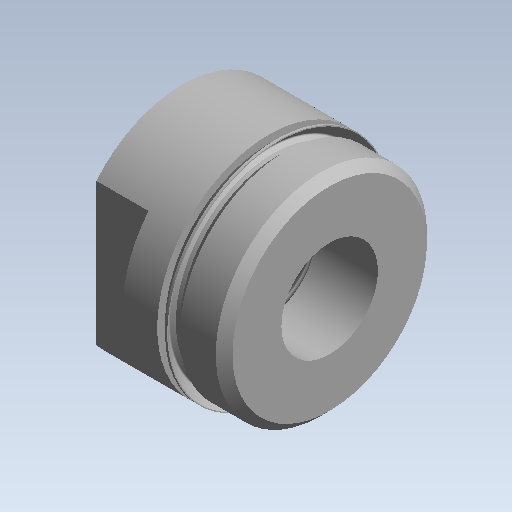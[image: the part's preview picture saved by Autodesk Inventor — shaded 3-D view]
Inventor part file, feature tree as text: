
AUTODESK INVENTOR PART (.ipt)
format: ipt  version: 2020 (Build 240168000, 168)  size: 226,304 bytes
history: native  units: mm (DEFAULTED — no unit token found)
features: other x126, sketch x4, revolve x3, thread x1, extrude x1
ambient origin geometry x8: Origin, YZ Plane, XZ Plane, XY Plane, X Axis, Y Axis, Z Axis, Center Point
bodies: Solid1 (feature_tree)
feature tree (135):
  revolve  "Revolution1"  Angle=360.0deg
  revolve  "Revolution2"  [1 undecoded]
  thread  "Thread1"  [1 undecoded]
  extrude  "Extrusion1"  [1 undecoded]
  revolve  "Revolution3"  [1 undecoded]
  other  "cut1_XY"
  other  "cut1_YZ"
  other  "cut1_ZX"
  other  "cut1_X"
  other  "cut1_Y"
  other  "cut1_Z"
  other  "cut1_Center"
  other  "cut2_XY"
  other  "cut2_YZ"
  other  "cut2_ZX"
  other  "cut2_X"
  other  "cut2_Y"
  other  "cut2_Z"
  other  "cut2_Center"
  other  "cutf1_XY"
  other  "cutf1_YZ"
  other  "cutf1_ZX"
  other  "cutf1_X"
  other  "cutf1_Y"
  other  "cutf1_Z"
  other  "cutf1_Center"
  other  "cutf2_XY"
  other  "cutf2_YZ"
  other  "cutf2_ZX"
  other  "cutf2_X"
  other  "cutf2_Y"
  other  "cutf2_Z"
  other  "cutf2_Center"
  other  "lovra_XY"
  other  "lovra_YZ"
  other  "lovra_ZX"
  other  "lovra_X"
  other  "lovra_Y"
  other  "lovra_Z"
  other  "lovra_Center"
  other  "lovra1_XY"
  other  "lovra1_YZ"
  other  "lovra1_ZX"
  other  "lovra1_X"
  other  "lovra1_Y"
  other  "lovra1_Z"
  other  "lovra1_Center"
  other  "lovra2_XY"
  other  "lovra2_YZ"
  other  "lovra2_ZX"
  other  "lovra2_X"
  other  "lovra2_Y"
  other  "lovra2_Z"
  other  "lovra2_Center"
  other  "lovra21_XY"
  other  "lovra21_YZ"
  other  "lovra21_ZX"
  other  "lovra21_X"
  other  "lovra21_Y"
  other  "lovra21_Z"
  other  "lovra21_Center"
  other  "lovra22_XY"
  other  "lovra22_YZ"
  other  "lovra22_ZX"
  other  "lovra22_X"
  other  "lovra22_Y"
  other  "lovra22_Z"
  other  "lovra22_Center"
  other  "lovra3_XY"
  other  "lovra3_YZ"
  other  "lovra3_ZX"
  other  "lovra3_X"
  other  "lovra3_Y"
  other  "lovra3_Z"
  other  "lovra3_Center"
  other  "olen_XY"
  other  "olen_YZ"
  other  "olen_ZX"
  other  "olen_X"
  other  "olen_Y"
  other  "olen_Z"
  other  "olen_Center"
  other  "to_mounting_bracket_XY"
  other  "to_mounting_bracket_YZ"
  other  "to_mounting_bracket_ZX"
  other  "to_mounting_bracket_X"
  other  "to_mounting_bracket_Y"
  other  "to_mounting_bracket_Z"
  other  "to_mounting_bracket_Center"
  other  "to_nut_XY"
  other  "to_nut_YZ"
  other  "to_nut_ZX"
  other  "to_nut_X"
  other  "to_nut_Y"
  other  "to_nut_Z"
  other  "to_nut_Center"
  other  "to_pin_XY"
  other  "to_pin_YZ"
  other  "to_pin_ZX"
  other  "to_pin_X"
  other  "to_pin_Y"
  other  "to_pin_Z"
  other  "to_pin_Center"
  other  "to_pin_1_XY"
  other  "to_pin_1_YZ"
  other  "to_pin_1_ZX"
  other  "to_pin_1_X"
  other  "to_pin_1_Y"
  other  "to_pin_1_Z"
  other  "to_pin_1_Center"
  other  "to_pin_r_XY"
  other  "to_pin_r_YZ"
  other  "to_pin_r_ZX"
  other  "to_pin_r_X"
  other  "to_pin_r_Y"
  other  "to_pin_r_Z"
  other  "to_pin_r_Center"
  other  "to_screw_XY"
  other  "to_screw_YZ"
  other  "to_screw_ZX"
  other  "to_screw_X"
  other  "to_screw_Y"
  other  "to_screw_Z"
  other  "to_screw_Center"
  other  "to_tube_XY"
  other  "to_tube_YZ"
  other  "to_tube_ZX"
  other  "to_tube_X"
  other  "to_tube_Y"
  other  "to_tube_Z"
  other  "to_tube_Center"
  sketch  "Sketch_1"  dims[d0=360.0deg d1=360.0deg]
  sketch  "Sketch_6"  dims[d7=0.0mm d8=0.0mm d9=0.0mm d10=0.0mm d11=0.0mm d12=0.0mm d13=0.0mm d14=0.0mm d15=0.0mm d16=0.0mm]
  sketch  "Sketch_5"  dims[d2=7.03922mm d3=0.0mm d4=4.7752mm d5=0.0mm d6=360.0deg]
  sketch  "Sketch_24"
note: 4 required parameter values undecoded (feature->parameter linkage not recoverable at this tier; creation-order binding heuristic only, values carry confidence <= 0.55)